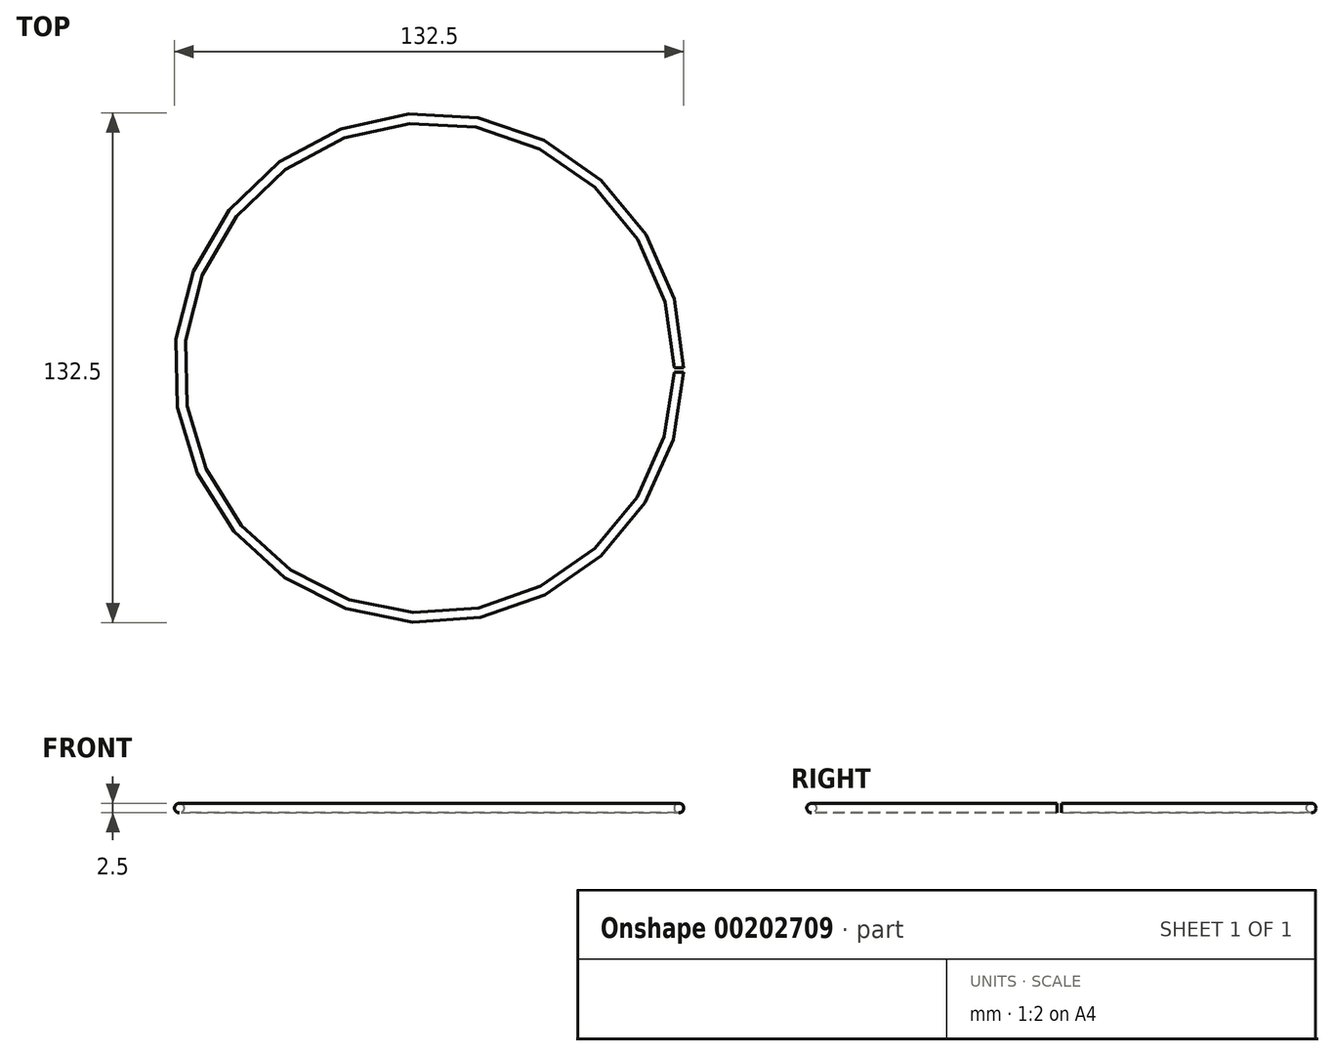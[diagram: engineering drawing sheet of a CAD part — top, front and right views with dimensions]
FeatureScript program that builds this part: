
annotation { "Feature Type Name" : "Feature", "Feature Type Description" : "" }
export const myFeature = defineFeature(function(context is Context, id is Id, definition is map)
    precondition{}
    {
        {
            var Q0;
            Q0=qCreatedBy(makeId("Front.planeOp"),FACE);
            var sketch = newSketch(context, id + "F0", { "sketchPlane" : qUnion([Q0])});
            skLineSegment(sketch, "E0", {"start": v(0, 0) * mm, "end": v(0, 36.67) * mm});
            skCircle(sketch, "E1", {"center": v(65, 0) * mm, "radius": 1.25 * mm});
            skSolve(sketch);
        }
        {
            var Q0;
            Q0=makeQuery(id+"F0.imprint","IMPRINT",FACE,{"disambiguationData":[TD([[makeQuery(id+"F0.imprint","IMPRINT",EDGE,{"derivedFrom":sQuery(id+"F0.wireOp",EDGE,"E1")}),1.0]])]});
            var Q1;
            Q1=sQuery(id+"F0.wireOp",EDGE,"E0");
            revolve(context, id + "F1", {"entities" : qUnion([Q0]), "axis" : qUnion([Q1]), "revolveType" : RevolveType.ONE_DIRECTION, "angle" : 359 * degree});
        }
    });
